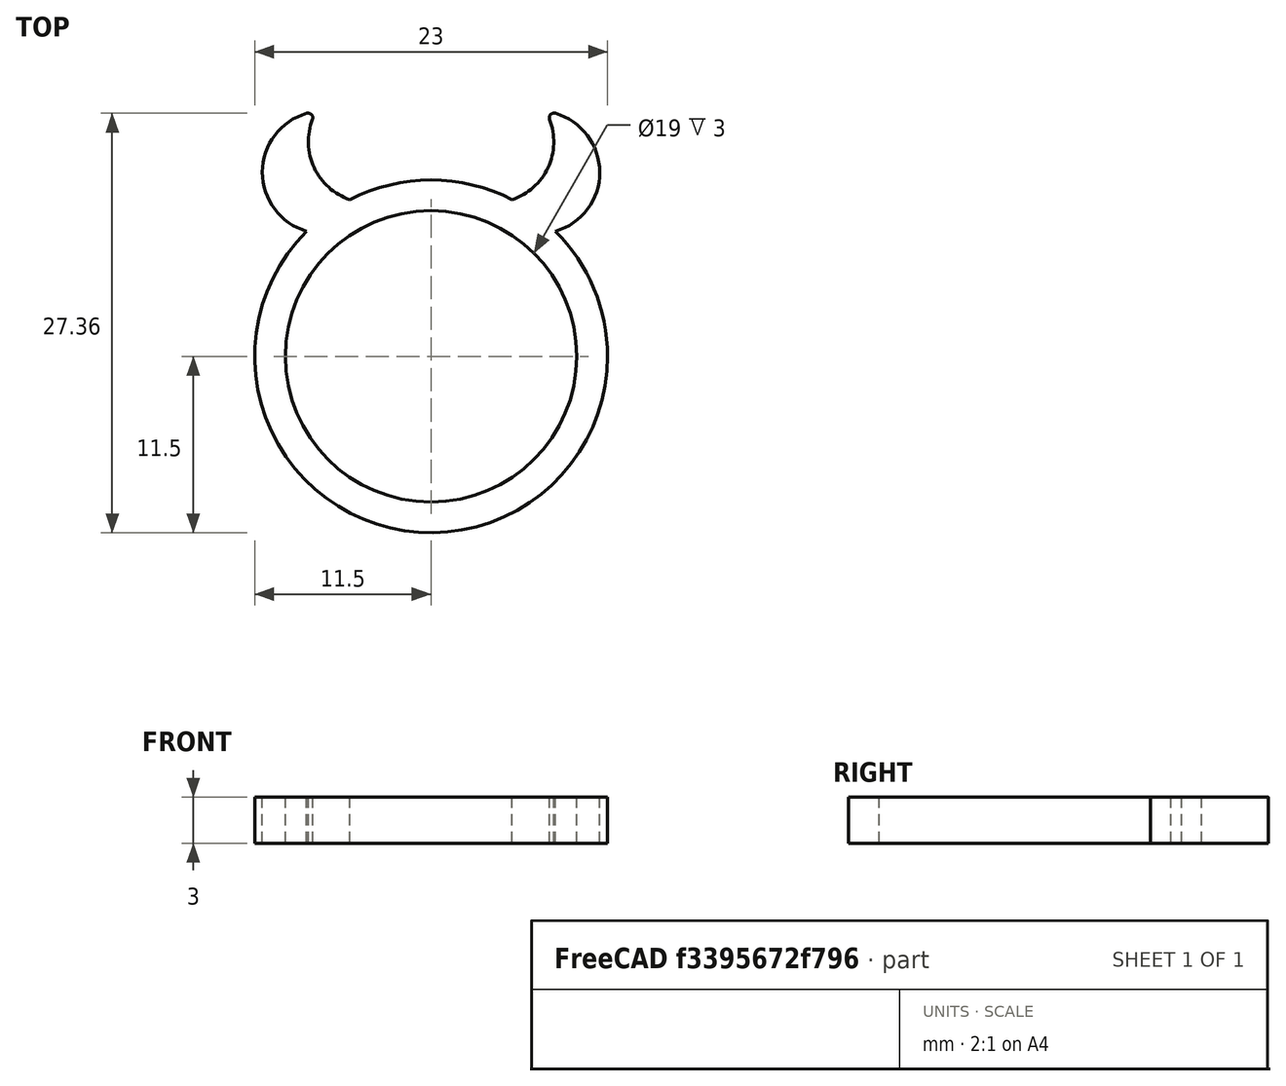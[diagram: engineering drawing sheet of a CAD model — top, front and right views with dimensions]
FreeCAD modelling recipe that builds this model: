
FCSTD DOCUMENT  (FreeCAD 0.16R6707 (Git))
Label: anillo-diablillo
License: All rights reserved
LicenseURL: http://en.wikipedia.org/wiki/All_rights_reserved
objects: Part::Cylinder×4, Part::Cut×3, Part::Mirroring×1, Part::MultiFuse×1, Part::Fillet×1
note: 10 computed .brp shape members not serialized (recipe doc carries the construction recipe); baked Part::Feature solids carry a one-line shape summary decoded from their .brp

FEATURE [Part::Cylinder] Cylinder  label="cilindro-exterior"
  Angle = 360
  Height = 3
  Radius = 11.5
  expr: Radius = 23 / 2
FEATURE [Part::Cylinder] Cylinder001  label="cilindro-interior"
  Angle = 360
  Height = 10
  Placement = pos=(0,0,-3) rot=(0,0,1;0rad)
  Radius = 9.5
  expr: Radius = 19 / 2
FEATURE [Part::Cut] Cut  label="Cuerpo-anillo"
  Base = -> Cylinder
  Tool = -> Cylinder001
FEATURE [Part::Cylinder] Cylinder002  label="Cilindro002"
  Angle = 360
  Height = 3
  Radius = 4
FEATURE [Part::Cylinder] Cylinder003  label="Cilindro003"
  Angle = 360
  Height = 3
  Placement = pos=(3,2,0) rot=(0,0,1;0rad)
  Radius = 4
FEATURE [Part::Cut] Cut001
  Base = -> Cylinder002
  Placement = pos=(-7,11,0) rot=(0,0,1;0rad)
  Tool = -> Cylinder003
FEATURE [Part::Cut] Cut002  label="Cuerno-izdo"
  Base = -> Cylinder002
  Placement = pos=(-7,12,0) rot=(0,0,1;0rad)
  Tool = -> Cylinder003
FEATURE [Part::Mirroring] Part__Mirroring  label="Cuerno-decho"
  Base = (0,0,0)
  Normal = (1,0,0)
  Placement = pos=(0,1,0) rot=(0,0,1;0rad)
  Source = -> Cut001
FEATURE [Part::MultiFuse] Fusion  label="Anillo-sin-redondeo"
  Shapes = -> [Cut002,Part__Mirroring,Cut]
FEATURE [Part::Fillet] Fillet  label="Anillo-final"
  Base = -> Fusion
  Edges = 2 edges r=0.3: [Edge7,Edge13]
